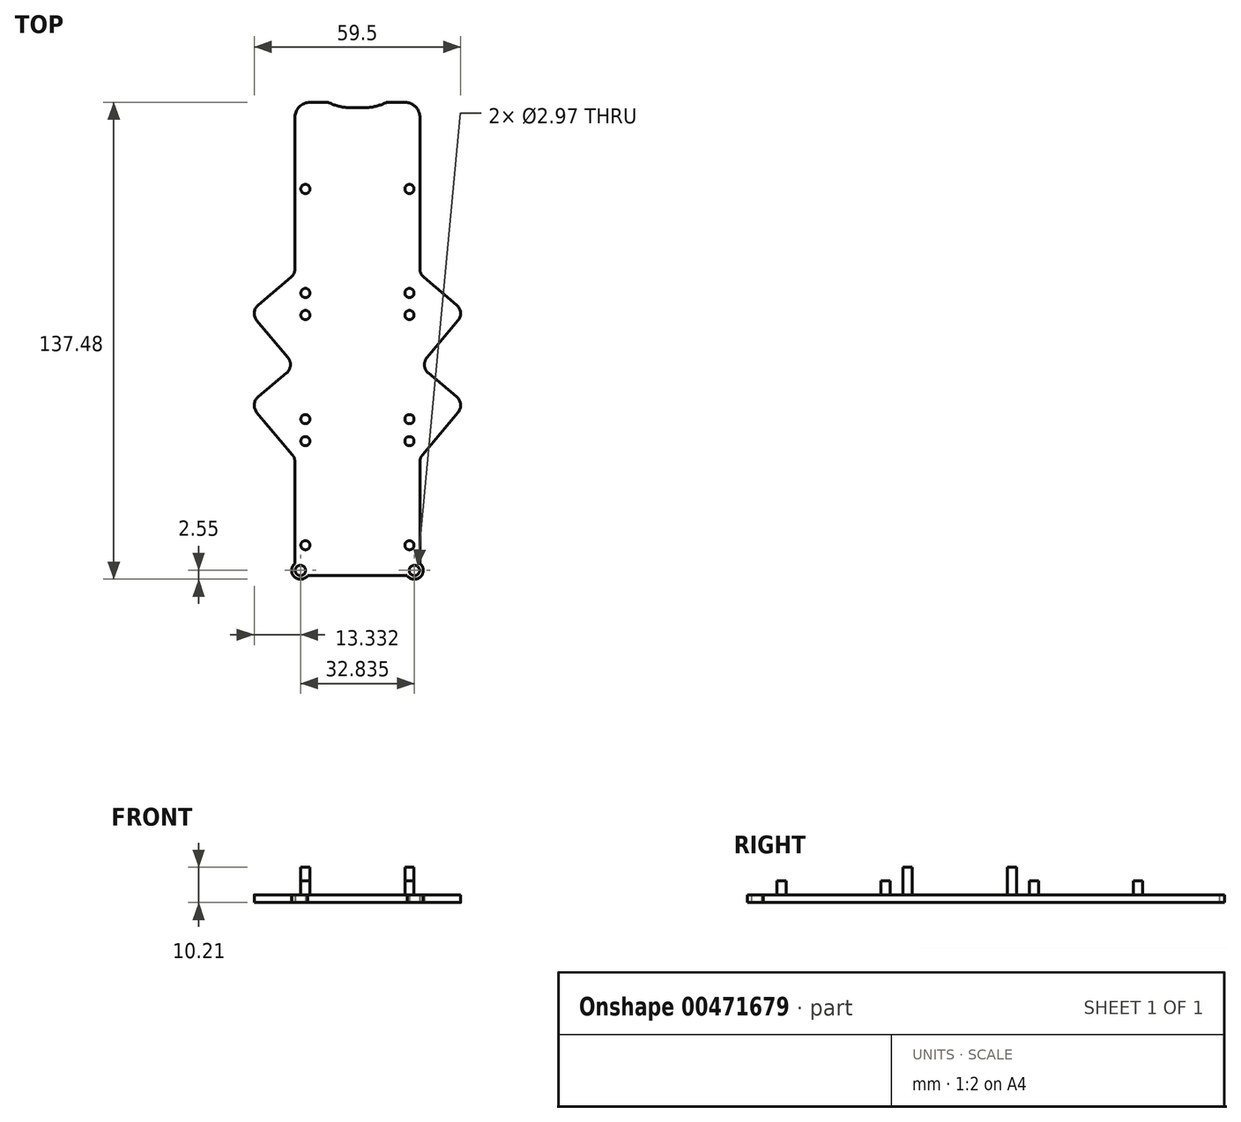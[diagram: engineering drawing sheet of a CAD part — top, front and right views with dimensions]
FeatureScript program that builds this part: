
annotation { "Feature Type Name" : "Feature", "Feature Type Description" : "" }
export const myFeature = defineFeature(function(context is Context, id is Id, definition is map)
    precondition{}
    {
        {
            var Q0;
            Q0=qCreatedBy(makeId("Top.planeOp"),FACE);
            var sketch = newSketch(context, id + "F0", { "sketchPlane" : qUnion([Q0])});
            skLineSegment(sketch, "E0.bottom", {"start": v(-2.11, 67.47) * mm, "end": v(2.11, 67.47) * mm});
            skLineSegment(sketch, "E0.top", {"start": v(-14.37, -67.47) * mm, "end": v(14.37, -67.47) * mm});
            skLineSegment(sketch, "E0.left", {"start": v(-18.01, 67.47) * mm, "end": v(-18.01, 20.94) * mm});
            skLineSegment(sketch, "E0.right", {"start": v(18.01, 67.47) * mm, "end": v(18.01, 20.94) * mm});
            skPoint(sketch, "E0.middle", {"position": v(0, 0) * mm});
            skLineSegment(sketch, "E1", {"start": v(-13.7, 69) * mm, "end": v(-8.74, 69) * mm});
            skLineSegment(sketch, "E2", {"start": v(-8.22, 68.88) * mm, "end": v(-7.78, 68.69) * mm});
            skLineSegment(sketch, "E3", {"start": v(13.7, 69) * mm, "end": v(8.74, 69) * mm});
            skLineSegment(sketch, "E4", {"start": v(8.22, 68.88) * mm, "end": v(7.78, 68.69) * mm});
            skLineSegment(sketch, "E5", {"start": v(-18.01, 67.47) * mm, "end": v(-18.01, 64.67) * mm});
            skLineSegment(sketch, "E6", {"start": v(18.01, 67.47) * mm, "end": v(18.01, 64.67) * mm});
            skPoint(sketch, "E7.visualSharp", {"position": v(-18.01, 69) * mm});
            skArc(sketch, "E7.filletArc", {"start": v(-13.7, 69) * mm, "mid": v(-16.75, 67.73) * mm, "end": v(-18.01, 64.67) * mm});
            skPoint(sketch, "E8.visualSharp", {"position": v(18.01, 69) * mm});
            skArc(sketch, "E8.filletArc", {"start": v(18.01, 64.67) * mm, "mid": v(16.75, 67.73) * mm, "end": v(13.7, 69) * mm});
            skPoint(sketch, "E9.visualSharp", {"position": v(8.46, 69) * mm});
            skPoint(sketch, "E10.visualSharp", {"position": v(-8.46, 69) * mm});
            skPoint(sketch, "E11.visualSharp", {"position": v(-5.08, 67.47) * mm});
            skArc(sketch, "E11.filletArc", {"start": v(-7.78, 68.69) * mm, "mid": v(-5.01, 67.78) * mm, "end": v(-2.11, 67.47) * mm});
            skPoint(sketch, "E12.visualSharp", {"position": v(5.08, 67.47) * mm});
            skArc(sketch, "E12.filletArc", {"start": v(2.11, 67.47) * mm, "mid": v(5.01, 67.78) * mm, "end": v(7.78, 68.69) * mm});
            skArc(sketch, "E13.filletArc", {"start": v(-8.22, 68.88) * mm, "mid": v(-8.47, 68.96) * mm, "end": v(-8.74, 69) * mm});
            skArc(sketch, "E14.filletArc", {"start": v(8.74, 69) * mm, "mid": v(8.47, 68.96) * mm, "end": v(8.22, 68.88) * mm});
            skLineSegment(sketch, "E15", {"start": v(19.15, 18.51) * mm, "end": v(28.62, 10.57) * mm});
            skLineSegment(sketch, "E16", {"start": v(29.01, 6.1) * mm, "end": v(20.06, -4.58) * mm});
            skLineSegment(sketch, "E17", {"start": v(20.45, -9.06) * mm, "end": v(28.62, -15.91) * mm});
            skLineSegment(sketch, "E18", {"start": v(29.01, -20.39) * mm, "end": v(18.76, -32.61) * mm});
            skPoint(sketch, "E19.visualSharp", {"position": v(18.01, -7.02) * mm});
            skArc(sketch, "E19.filletArc", {"start": v(20.06, -4.58) * mm, "mid": v(19.33, -6.9) * mm, "end": v(20.45, -9.06) * mm});
            skPoint(sketch, "E20.visualSharp", {"position": v(31.05, -17.95) * mm});
            skArc(sketch, "E20.filletArc", {"start": v(29.01, -20.39) * mm, "mid": v(29.74, -18.07) * mm, "end": v(28.62, -15.91) * mm});
            skLineSegment(sketch, "E21.trimOffspring", {"start": v(18.01, -34.65) * mm, "end": v(18.01, -63.95) * mm});
            skPoint(sketch, "E22.visualSharp", {"position": v(31.05, 8.53) * mm});
            skArc(sketch, "E22.filletArc", {"start": v(29.01, 6.1) * mm, "mid": v(29.74, 8.41) * mm, "end": v(28.62, 10.57) * mm});
            skPoint(sketch, "E23.visualSharp", {"position": v(18.01, 19.46) * mm});
            skArc(sketch, "E23.filletArc", {"start": v(18.01, 20.94) * mm, "mid": v(18.31, 19.6) * mm, "end": v(19.15, 18.51) * mm});
            skPoint(sketch, "E24.visualSharp", {"position": v(18.01, -33.5) * mm});
            skArc(sketch, "E24.filletArc", {"start": v(18.76, -32.61) * mm, "mid": v(18.2, -33.57) * mm, "end": v(18.01, -34.65) * mm});
            skLineSegment(sketch, "E25.MirrorCS", {"start": v(-19.15, 18.51) * mm, "end": v(-28.62, 10.57) * mm});
            skArc(sketch, "E26.MirrorCS", {"start": v(-18.01, 20.94) * mm, "mid": v(-18.31, 19.6) * mm, "end": v(-19.15, 18.51) * mm});
            skArc(sketch, "E27.MirrorCS", {"start": v(-29.01, 6.1) * mm, "mid": v(-29.74, 8.41) * mm, "end": v(-28.62, 10.57) * mm});
            skLineSegment(sketch, "E28.MirrorCS", {"start": v(-29.01, 6.1) * mm, "end": v(-20.06, -4.58) * mm});
            skLineSegment(sketch, "E29.MirrorCS", {"start": v(-20.45, -9.06) * mm, "end": v(-28.62, -15.91) * mm});
            skArc(sketch, "E30.MirrorCS", {"start": v(-20.06, -4.58) * mm, "mid": v(-19.33, -6.9) * mm, "end": v(-20.45, -9.06) * mm});
            skArc(sketch, "E31.MirrorCS", {"start": v(-29.01, -20.39) * mm, "mid": v(-29.74, -18.07) * mm, "end": v(-28.62, -15.91) * mm});
            skLineSegment(sketch, "E32.MirrorCS", {"start": v(-29.01, -20.39) * mm, "end": v(-18.76, -32.61) * mm});
            skArc(sketch, "E33.MirrorCS", {"start": v(-18.76, -32.61) * mm, "mid": v(-18.2, -33.57) * mm, "end": v(-18.01, -34.65) * mm});
            skLineSegment(sketch, "E34.trimOffspring", {"start": v(-18.01, -34.65) * mm, "end": v(-18.01, -63.95) * mm});
            skCircle(sketch, "E35", {"center": v(-16.42, -65.94) * mm, "radius": 1.49 * mm});
            skCircle(sketch, "E36", {"center": v(-16.42, -65.94) * mm, "radius": 2.55 * mm});
            skLineSegment(sketch, "E37", {"start": v(-18.01, -67.47) * mm, "end": v(-15.32, -64.77) * mm, "construction": true});
            skCircle(sketch, "E38.MirrorC", {"center": v(16.42, -65.94) * mm, "radius": 2.55 * mm});
            skCircle(sketch, "E39.MirrorC", {"center": v(16.42, -65.94) * mm, "radius": 1.49 * mm});
            skPoint(sketch, "E40.orphan", {"position": v(18.01, -67.47) * mm});
            skSolve(sketch);
        }
        {
            var Q0;
            Q0 = qSketchRegion(id + "F0", true);
            extrude(context, id + "F1", {"entities" : qUnion([Q0]), "depth" : 2.2 * mm});
        }
        {
            var Q0;
            Q0=makeQuery(id+"F1.opExtrude","CAP_FACE",FACE,{"disambiguationData":[OSD([sQuery(id+"F0.wireOp",EDGE,"E0.top"),sQuery(id+"F0.wireOp",EDGE,"E0.left"),sQuery(id+"F0.wireOp",EDGE,"E0.right"),sQuery(id+"F0.wireOp",EDGE,"E0.bottom"),sQuery(id+"F0.wireOp",EDGE,"E1"),sQuery(id+"F0.wireOp",EDGE,"E2"),sQuery(id+"F0.wireOp",EDGE,"E3"),sQuery(id+"F0.wireOp",EDGE,"E4"),sQuery(id+"F0.wireOp",EDGE,"E7.filletArc"),sQuery(id+"F0.wireOp",EDGE,"E8.filletArc"),sQuery(id+"F0.wireOp",EDGE,"E11.filletArc"),sQuery(id+"F0.wireOp",EDGE,"E12.filletArc"),sQuery(id+"F0.wireOp",EDGE,"E13.filletArc"),sQuery(id+"F0.wireOp",EDGE,"E14.filletArc"),sQuery(id+"F0.wireOp",EDGE,"E15"),sQuery(id+"F0.wireOp",EDGE,"E16"),sQuery(id+"F0.wireOp",EDGE,"E17"),sQuery(id+"F0.wireOp",EDGE,"E18"),sQuery(id+"F0.wireOp",EDGE,"E19.filletArc"),sQuery(id+"F0.wireOp",EDGE,"E20.filletArc"),sQuery(id+"F0.wireOp",EDGE,"E21.trimOffspring"),sQuery(id+"F0.wireOp",EDGE,"E22.filletArc"),sQuery(id+"F0.wireOp",EDGE,"E23.filletArc"),sQuery(id+"F0.wireOp",EDGE,"E24.filletArc"),sQuery(id+"F0.wireOp",EDGE,"E25.MirrorCS"),sQuery(id+"F0.wireOp",EDGE,"E26.MirrorCS"),sQuery(id+"F0.wireOp",EDGE,"E27.MirrorCS"),sQuery(id+"F0.wireOp",EDGE,"E28.MirrorCS"),sQuery(id+"F0.wireOp",EDGE,"E29.MirrorCS"),sQuery(id+"F0.wireOp",EDGE,"E30.MirrorCS"),sQuery(id+"F0.wireOp",EDGE,"E31.MirrorCS"),sQuery(id+"F0.wireOp",EDGE,"E32.MirrorCS"),sQuery(id+"F0.wireOp",EDGE,"E33.MirrorCS"),sQuery(id+"F0.wireOp",EDGE,"E34.trimOffspring"),sQuery(id+"F0.wireOp",EDGE,"E35"),sQuery(id+"F0.wireOp",EDGE,"E36"),sQuery(id+"F0.wireOp",EDGE,"E38.MirrorC"),sQuery(id+"F0.wireOp",EDGE,"E39.MirrorC")])],"isStart":false});
            var sketch = newSketch(context, id + "F2", { "sketchPlane" : qUnion([Q0])});
            skCircle(sketch, "E41", {"center": v(-15, 7.67) * mm, "radius": 1.33 * mm});
            skCircle(sketch, "E42", {"center": v(15, 7.67) * mm, "radius": 1.33 * mm});
            skCircle(sketch, "E43", {"center": v(15, -22.33) * mm, "radius": 1.33 * mm});
            skCircle(sketch, "E44", {"center": v(-15, -22.33) * mm, "radius": 1.33 * mm});
            skCircle(sketch, "E45", {"center": v(-15, -28.68) * mm, "radius": 1.33 * mm});
            skCircle(sketch, "E46", {"center": v(15, -28.68) * mm, "radius": 1.33 * mm});
            skCircle(sketch, "E47", {"center": v(15, -58.68) * mm, "radius": 1.33 * mm});
            skCircle(sketch, "E48", {"center": v(-15, -58.68) * mm, "radius": 1.33 * mm});
            skCircle(sketch, "E49", {"center": v(-15, 44.02) * mm, "radius": 1.33 * mm});
            skCircle(sketch, "E50", {"center": v(15, 44.02) * mm, "radius": 1.33 * mm});
            skCircle(sketch, "E51", {"center": v(15, 14.02) * mm, "radius": 1.33 * mm});
            skCircle(sketch, "E52", {"center": v(-15, 14.02) * mm, "radius": 1.33 * mm});
            skLineSegment(sketch, "E53", {"start": v(-15, 7.67) * mm, "end": v(15, -22.33) * mm, "construction": true});
            skLineSegment(sketch, "E54", {"start": v(-15, -22.33) * mm, "end": v(15, 7.67) * mm, "construction": true});
            skLineSegment(sketch, "E55", {"start": v(-19.4, -7.33) * mm, "end": v(19.4, -7.33) * mm, "construction": true});
            skPoint(sketch, "E55.startSnap0", {"position": v(0, -7.33) * mm});
            skSolve(sketch);
        }
        {
            var Q0;
            Q0=makeQuery(id+"F2.imprint","IMPRINT",FACE,{"disambiguationData":[TD([[makeQuery(id+"F2.imprint","IMPRINT",EDGE,{"derivedFrom":sQuery(id+"F2.wireOp",EDGE,"E49")}),1.0]])]});
            var Q1;
            Q1=makeQuery(id+"F2.imprint","IMPRINT",FACE,{"disambiguationData":[TD([[makeQuery(id+"F2.imprint","IMPRINT",EDGE,{"derivedFrom":sQuery(id+"F2.wireOp",EDGE,"E50")}),1.0]])]});
            var Q2;
            Q2=makeQuery(id+"F2.imprint","IMPRINT",FACE,{"disambiguationData":[TD([[makeQuery(id+"F2.imprint","IMPRINT",EDGE,{"derivedFrom":sQuery(id+"F2.wireOp",EDGE,"E51")}),1.0]])]});
            var Q3;
            Q3=makeQuery(id+"F2.imprint","IMPRINT",FACE,{"disambiguationData":[TD([[makeQuery(id+"F2.imprint","IMPRINT",EDGE,{"derivedFrom":sQuery(id+"F2.wireOp",EDGE,"E52")}),1.0]])]});
            var Q4;
            Q4=makeQuery(id+"F2.imprint","IMPRINT",FACE,{"disambiguationData":[TD([[makeQuery(id+"F2.imprint","IMPRINT",EDGE,{"derivedFrom":sQuery(id+"F2.wireOp",EDGE,"E46")}),1.0]])]});
            var Q5;
            Q5=makeQuery(id+"F2.imprint","IMPRINT",FACE,{"disambiguationData":[TD([[makeQuery(id+"F2.imprint","IMPRINT",EDGE,{"derivedFrom":sQuery(id+"F2.wireOp",EDGE,"E45")}),1.0]])]});
            var Q6;
            Q6=makeQuery(id+"F2.imprint","IMPRINT",FACE,{"disambiguationData":[TD([[makeQuery(id+"F2.imprint","IMPRINT",EDGE,{"derivedFrom":sQuery(id+"F2.wireOp",EDGE,"E48")}),1.0]])]});
            var Q7;
            Q7=makeQuery(id+"F2.imprint","IMPRINT",FACE,{"disambiguationData":[TD([[makeQuery(id+"F2.imprint","IMPRINT",EDGE,{"derivedFrom":sQuery(id+"F2.wireOp",EDGE,"E47")}),1.0]])]});
            extrude(context, id + "F3", {"entities" : qUnion([Q0, Q1, Q2, Q3, Q4, Q5, Q6, Q7]), "operationType" : NewBodyOperationType.ADD, "depth" : 4 * mm});
        }
        {
            var Q0;
            Q0=makeQuery(id+"F2.imprint","IMPRINT",FACE,{"disambiguationData":[TD([[makeQuery(id+"F2.imprint","IMPRINT",EDGE,{"derivedFrom":sQuery(id+"F2.wireOp",EDGE,"E42")}),1.0]])]});
            var Q1;
            Q1=makeQuery(id+"F2.imprint","IMPRINT",FACE,{"disambiguationData":[TD([[makeQuery(id+"F2.imprint","IMPRINT",EDGE,{"derivedFrom":sQuery(id+"F2.wireOp",EDGE,"E43")}),1.0]])]});
            var Q2;
            Q2=makeQuery(id+"F2.imprint","IMPRINT",FACE,{"disambiguationData":[TD([[makeQuery(id+"F2.imprint","IMPRINT",EDGE,{"derivedFrom":sQuery(id+"F2.wireOp",EDGE,"E44")}),1.0]])]});
            var Q3;
            Q3=makeQuery(id+"F2.imprint","IMPRINT",FACE,{"disambiguationData":[TD([[makeQuery(id+"F2.imprint","IMPRINT",EDGE,{"derivedFrom":sQuery(id+"F2.wireOp",EDGE,"E41")}),1.0]])]});
            extrude(context, id + "F4", {"entities" : qUnion([Q0, Q1, Q2, Q3]), "operationType" : NewBodyOperationType.ADD, "depth" : 8 * mm});
        }
    });
